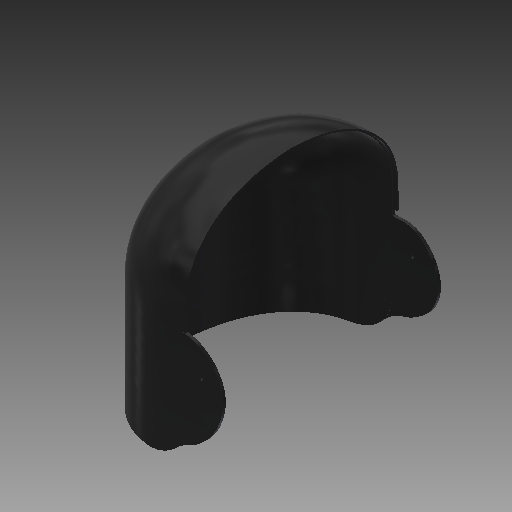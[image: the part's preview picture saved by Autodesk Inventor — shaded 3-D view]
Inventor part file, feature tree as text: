
AUTODESK INVENTOR PART (.ipt)
format: ipt  version: 2019 (Build 230136000, 136)  size: 686,080 bytes
history: native  units: mm
features: fillet x11, sketch x9, plane x8, extrude x6, projected_geometry x2, revolve x1, mirror x1
ambient origin geometry x8: Origin, YZ Plane, XZ Plane, XY Plane, X Axis, Y Axis, Z Axis, Center Point
bodies: Solid1 (feature_tree)
feature tree (38):
  plane  "Work Plane1"
  plane  "Work Plane2"
  plane  "Work Plane3"
  extrude  "Extrusion1"  Depth=1.5mm
  plane  "Work Plane4"
  extrude  "Extrusion2"  Depth=10.0mm
  fillet  "Fillet1"  Radius=10.0mm
  fillet  "Fillet2"  Radius=2.0mm
  fillet  "Fillet3"  Radius=2.0mm
  fillet  "Fillet4"  Radius=2.0mm
  fillet  "Fillet5"  Radius=2.0mm
  fillet  "Fillet6"  Radius=2.0mm
  fillet  "Fillet7"  Radius=2.0mm
  extrude  "Extrusion3"  TaperAngle=90.0deg  [1 undecoded]
  plane  "Work Plane5"
  sketch  "Sketch4"  dims[d17=90.0deg d18=100.0mm]
  sketch  "Sketch5"  dims[d19=180.0deg d23=90.0deg]
  plane  "Work Plane9"
  revolve  "Revolution2"  [1 undecoded]
  plane  "Work Plane11"
  extrude  "Extrusion4"  TaperAngle=90.0deg  [1 undecoded]
  mirror  "Mirror3"
  plane  "Work Plane12"
  extrude  "Extrusion5"  Depth=30.0mm TaperAngle=0.0deg
  fillet  "Fillet9"  Radius=30.0mm
  fillet  "Fillet10"  Radius=30.0mm
  fillet  "Fillet11"  Radius=30.0mm
  fillet  "Fillet12"  Radius=30.0mm
  extrude  "Extrusion6"  [1 undecoded]
  sketch  "Sketch1"  dims[d0=2.0mm d1=0.0mm d2=1.5mm]
  sketch  "Sketch2"  dims[d3=2.0mm d4=0.0mm d5=2.0mm d6=10.0mm d7=2.0mm d8=2.0mm d9=2.0mm d10=2.0mm d11=2.0mm d12=2.0mm d13=0.0mm]
  sketch  "Sketch3"  dims[d14=180.0deg d16=90.0deg]
  sketch  "Sketch6"  dims[d25=2.5mm d26=0.0mm d28=80.0mm d29=0.0mm d31=30.0mm d32=30.0mm d33=30.0mm d34=30.0mm]
  sketch  "Sketch8"  dims[d35=10.0mm d36=0.0mm]
  sketch  "Sketch11"
  projected_geometry  "Projected Loop4"
  sketch  "Sketch12"
  projected_geometry  "Projected Loop5"
note: 4 required parameter values undecoded (feature->parameter linkage not recoverable at this tier; creation-order binding heuristic only, values carry confidence <= 0.55)